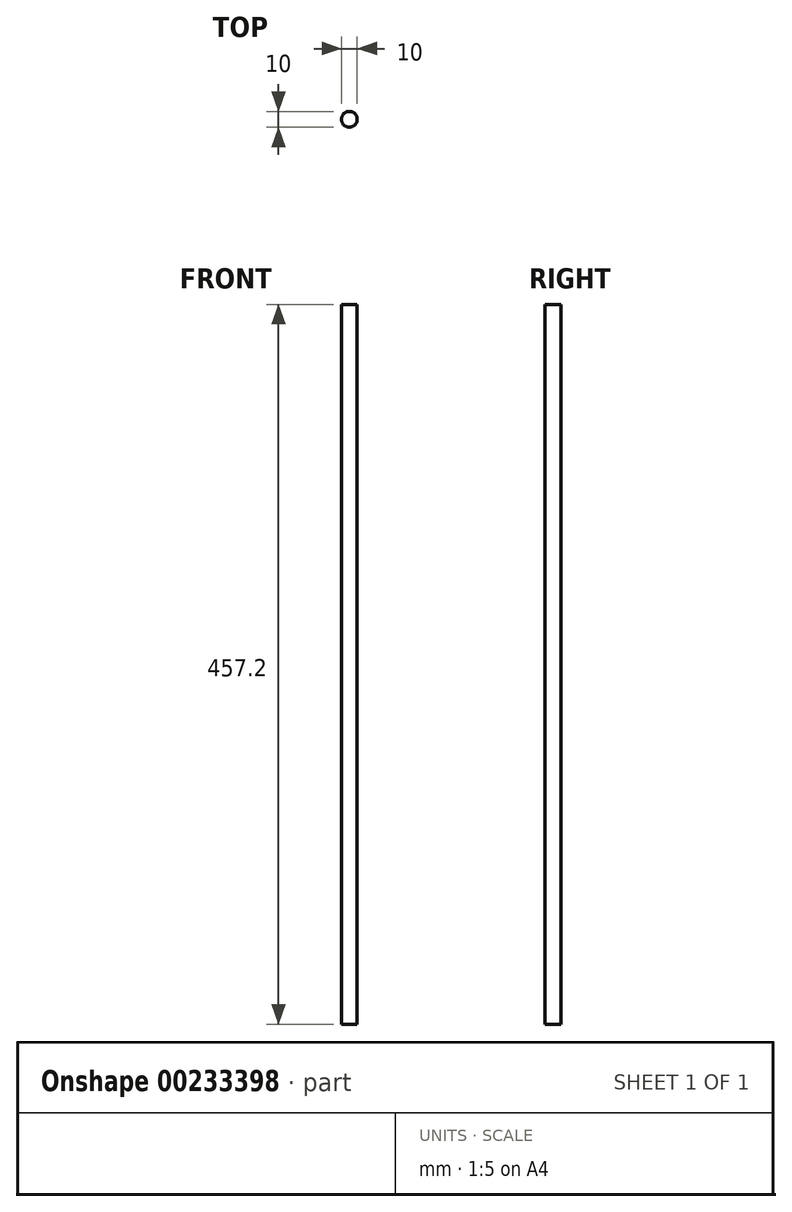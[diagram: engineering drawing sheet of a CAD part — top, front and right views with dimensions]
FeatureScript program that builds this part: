
annotation { "Feature Type Name" : "Feature", "Feature Type Description" : "" }
export const myFeature = defineFeature(function(context is Context, id is Id, definition is map)
    precondition{}
    {
        {
            var Q0;
            Q0=qCreatedBy(makeId("Top.planeOp"),FACE);
            var sketch = newSketch(context, id + "F0", { "sketchPlane" : qUnion([Q0])});
            skCircle(sketch, "E0", {"center": v(0, 0) * mm, "radius": 5 * mm});
            skSolve(sketch);
        }
        {
            var Q0;
            Q0=makeQuery(id+"F0.imprint","IMPRINT",FACE,{"disambiguationData":[TD([[makeQuery(id+"F0.imprint","IMPRINT",EDGE,{"derivedFrom":sQuery(id+"F0.wireOp",EDGE,"E0")}),1.0]])]});
            extrude(context, id + "F1", {"entities" : qUnion([Q0]), "depth" : 457.2 * mm});
        }
    });
